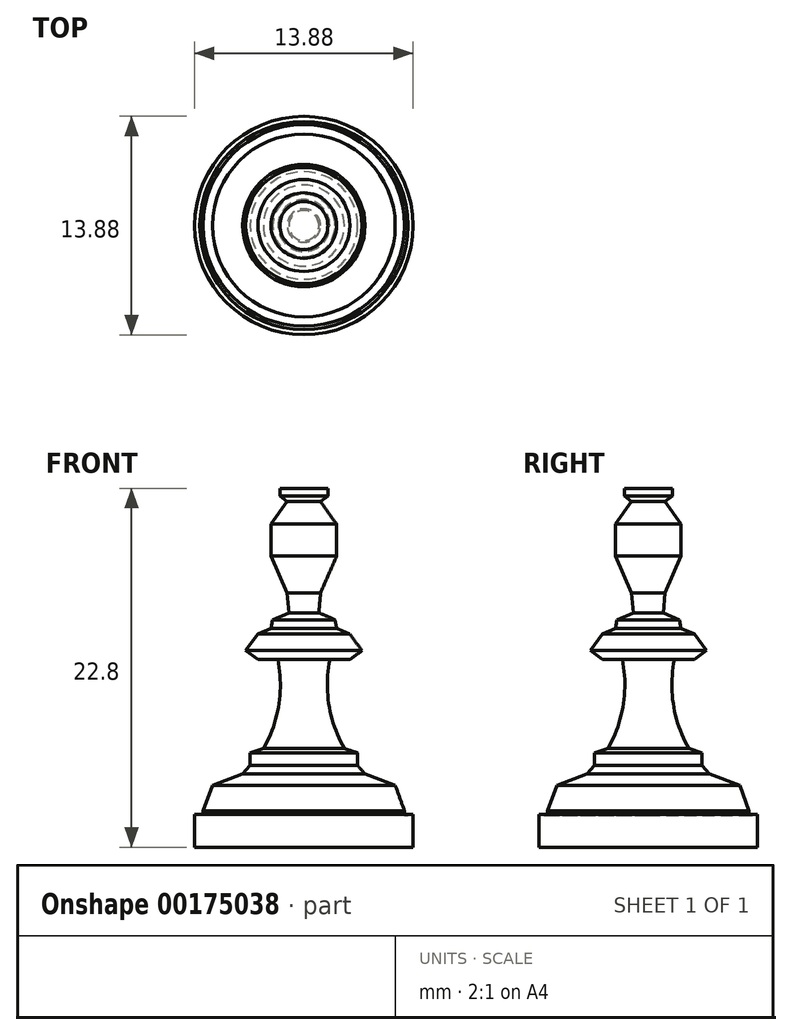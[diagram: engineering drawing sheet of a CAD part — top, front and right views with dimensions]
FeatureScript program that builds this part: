
annotation { "Feature Type Name" : "Feature", "Feature Type Description" : "" }
export const myFeature = defineFeature(function(context is Context, id is Id, definition is map)
    precondition{}
    {
        {
            var Q0;
            Q0=qCreatedBy(makeId("Front.planeOp"),FACE);
            var sketch = newSketch(context, id + "F0", { "sketchPlane" : qUnion([Q0])});
            skLineSegment(sketch, "E0", {"start": v(0, 46.4) * mm, "end": v(-1.52, 46.4) * mm});
            skLineSegment(sketch, "E1", {"start": v(-1.52, 46.4) * mm, "end": v(-1.52, 45.9) * mm});
            skLineSegment(sketch, "E2", {"start": v(-1.52, 45.9) * mm, "end": v(-1.06, 45.57) * mm});
            skLineSegment(sketch, "E3", {"start": v(-1.06, 45.57) * mm, "end": v(-2.08, 44.12) * mm});
            skLineSegment(sketch, "E4", {"start": v(-2.08, 44.12) * mm, "end": v(-2.08, 42.09) * mm});
            skLineSegment(sketch, "E5", {"start": v(-2.08, 42.09) * mm, "end": v(-1.06, 39.76) * mm});
            skLineSegment(sketch, "E6", {"start": v(-1.06, 39.76) * mm, "end": v(-0.95, 38.5) * mm});
            skLineSegment(sketch, "E7", {"start": v(-0.95, 38.5) * mm, "end": v(-1.98, 38.04) * mm});
            skLineSegment(sketch, "E8", {"start": v(-1.98, 38.04) * mm, "end": v(-2.08, 37.5) * mm});
            skLineSegment(sketch, "E9", {"start": v(-2.08, 37.5) * mm, "end": v(-2.92, 37.14) * mm});
            skLineSegment(sketch, "E10", {"start": v(-2.92, 37.14) * mm, "end": v(-3.7, 36.09) * mm});
            skLineSegment(sketch, "E11", {"start": v(-3.7, 36.09) * mm, "end": v(-2.92, 35.52) * mm});
            skLineSegment(sketch, "E12", {"start": v(-2.92, 35.52) * mm, "end": v(-1.65, 35.52) * mm});
            skArc(sketch, "E13", {"start": v(-2.57, 29.87) * mm, "mid": v(-1.6, 32.61) * mm, "end": v(-1.65, 35.52) * mm});
            skLineSegment(sketch, "E14", {"start": v(-2.57, 29.87) * mm, "end": v(-3.41, 29.6) * mm});
            skLineSegment(sketch, "E15", {"start": v(-3.41, 29.6) * mm, "end": v(-3.41, 28.79) * mm});
            skLineSegment(sketch, "E16", {"start": v(-3.41, 28.79) * mm, "end": v(-3.89, 28.25) * mm});
            skLineSegment(sketch, "E17", {"start": v(-3.89, 28.25) * mm, "end": v(-5.8, 27.54) * mm});
            skLineSegment(sketch, "E18", {"start": v(-5.8, 27.54) * mm, "end": v(-6.4, 25.9) * mm});
            skLineSegment(sketch, "E19", {"start": v(-6.4, 25.9) * mm, "end": v(-6.4, 25.6) * mm});
            skLineSegment(sketch, "E20", {"start": v(-6.4, 25.6) * mm, "end": v(-6.61, 25.62) * mm});
            skLineSegment(sketch, "E21", {"start": v(-6.61, 25.68) * mm, "end": v(-6.61, 25.62) * mm});
            skLineSegment(sketch, "E22", {"start": v(-6.61, 25.68) * mm, "end": v(-6.94, 25.69) * mm});
            skLineSegment(sketch, "E23", {"start": v(-6.94, 25.69) * mm, "end": v(-6.94, 25.69) * mm});
            skLineSegment(sketch, "E24", {"start": v(-6.94, 25.69) * mm, "end": v(-6.94, 23.6) * mm});
            skLineSegment(sketch, "E25", {"start": v(-6.94, 23.6) * mm, "end": v(0, 23.6) * mm});
            skLineSegment(sketch, "E26", {"start": v(0, 46.4) * mm, "end": v(0, 23.6) * mm});
            skSolve(sketch);
        }
        {
            var Q0;
            Q0 = qSketchRegion(id + "F0", true);
            var Q1;
            Q1=sQuery(id+"F0.wireOp",EDGE,"E26");
            revolve(context, id + "F1", {"entities" : qUnion([Q0]), "axis" : qUnion([Q1]), "revolveType" : RevolveType.FULL});
        }
    });
